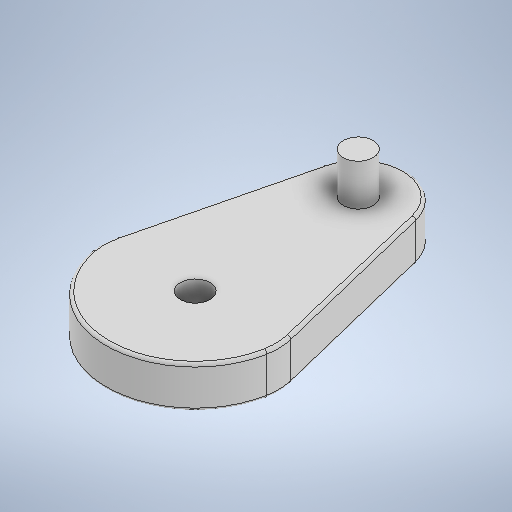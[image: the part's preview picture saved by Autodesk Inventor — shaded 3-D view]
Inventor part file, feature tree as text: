
AUTODESK INVENTOR PART (.ipt)
format: ipt  version: 2025.1 (Build 291241000, 241)  size: 278,016 bytes
history: native  units: mm
features: extrude x2, fillet x2, sketch x1
ambient origin geometry x8: Origin, YZ Plane, XZ Plane, XY Plane, X Axis, Y Axis, Z Axis, Center Point
bodies: Solid1 (feature_tree), Solid2 (feature_tree)
feature tree (5):
  sketch  "Sketch1"  dims[d0=8.0mm d1=15.0mm d2=27.5mm d3=5.0mm d6=7.0mm d7=0.0mm d8=10.0mm d9=0.5mm d10=5.0mm d11=7.0mm d12=0.0mm]
  extrude  "Extrusion1"  Depth=15.0mm
  fillet  "Fillet1"  Radius=27.5mm
  fillet  "Fillet2"  Radius=5.0mm
  extrude  "Extrusion2"  Depth=7.0mm TaperAngle=0.0deg
